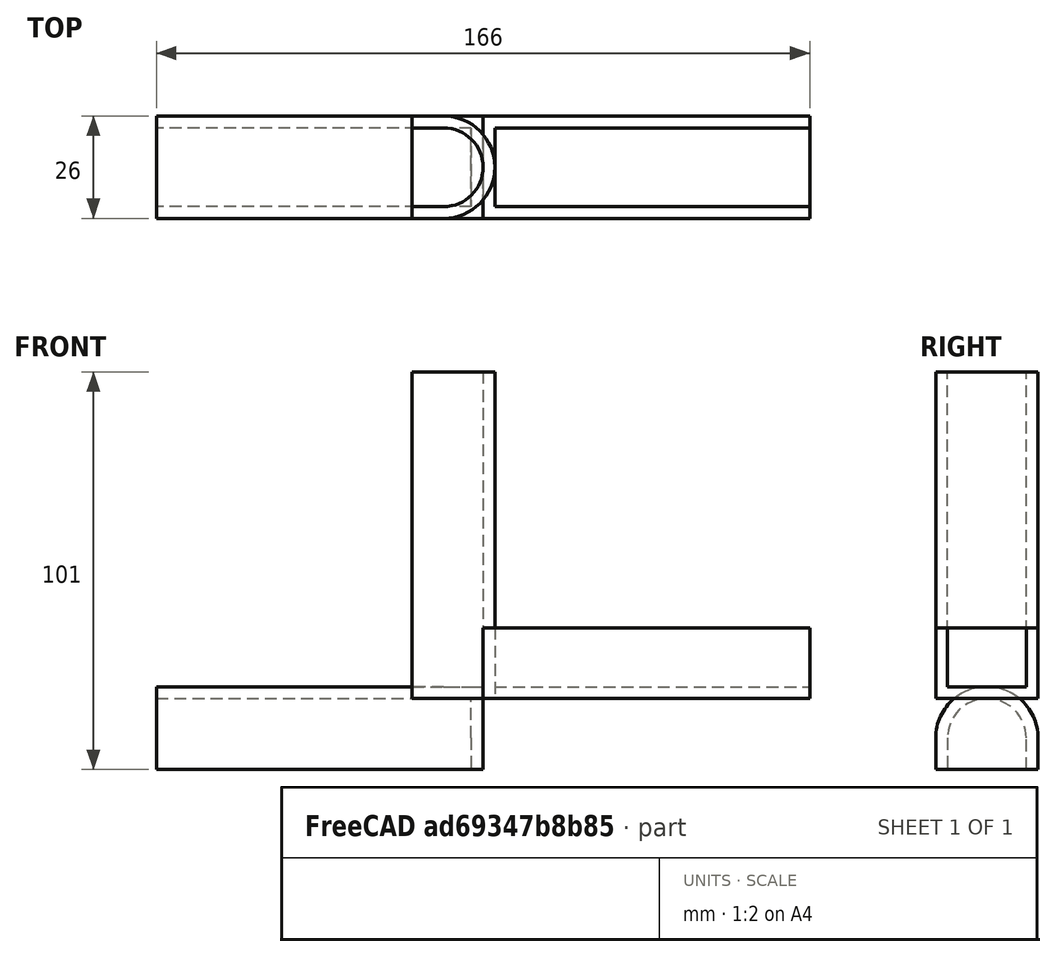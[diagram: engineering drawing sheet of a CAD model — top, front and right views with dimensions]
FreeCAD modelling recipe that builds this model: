
FCSTD DOCUMENT  (FreeCAD 0.16R6704 (Git))
Label: Peça
License: All rights reserved
LicenseURL: http://en.wikipedia.org/wiki/All_rights_reserved
objects: Part::Box×5, Part::Cylinder×3, Part::MultiFuse×2, Part::Feature×2, Part::Cut×2
note: 14 computed .brp shape members not serialized (recipe doc carries the construction recipe); baked Part::Feature solids carry a one-line shape summary decoded from their .brp

FEATURE [Part::Box] Box  label="BaseInferior"
  Height = 3
  Length = 83
  Width = 26
FEATURE [Part::Box] Box001  label="ParedeEsquerda"
  Height = 18
  Length = 83
  Width = 3
FEATURE [Part::Box] Box002  label="ParedeDireita"
  Height = 18
  Length = 83
  Placement = pos=(0,23,0) rot=(0,0,1;0rad)
  Width = 3
FEATURE [Part::Box] Box003  label="ParedeFundo"
  Height = 18
  Length = 3
  Width = 26
FEATURE [Part::MultiFuse] Fusion  label="Peça Unida - Sem Refinar"
  Shapes = -> [Box002,Box003,Box,Box001]
FEATURE [Part::Feature] Fusion001  label="Peça Final - Refinada - Sem Curvas"
  Placement = pos=(0,0,0) rot=(0,1,0;3.14159rad)
  shape: bbox 83 x 26 x 18 mm, 10 faces (baked)
FEATURE [Part::Cylinder] Cylinder  label="Cilindro"
  Angle = 180
  Height = 83
  Placement = pos=(-83,13,0) rot=(0.57735,0.57735,0.57735;2.0944rad)
  Radius = 13
FEATURE [Part::Cylinder] Cylinder001  label="Cilindro001"
  Angle = 180
  Height = 83
  Placement = pos=(-83,13,0) rot=(0.57735,0.57735,0.57735;2.0944rad)
  Radius = 10
FEATURE [Part::Cut] Cut
  Base = -> Cylinder
  Placement = pos=(0,0,-10) rot=(0,0,1;0rad)
  Tool = -> Cylinder001
FEATURE [Part::Box] Box004  label="Cubo"
  Height = 25
  Length = 83
  Placement = pos=(-83,0,-10) rot=(0,0,1;0rad)
  Width = 26
FEATURE [Part::Cut] Cut001
  Base = -> Fusion001
  Tool = -> Box004
FEATURE [Part::Cylinder] Cylinder002  label="Cilindro002"
  Angle = 180
  Height = 3
  Placement = pos=(-3,13,-10) rot=(0.57735,0.57735,0.57735;2.0944rad)
  Radius = 13
FEATURE [Part::MultiFuse] Fusion002
  Shapes = -> [Cylinder002,Cut001,Cut]
FEATURE [Part::Feature] Fusion002001  label="Fusion003"
  Placement = pos=(0,0,0) rot=(0,1,0;1.5708rad)
  shape: bbox 21 x 26 x 83 mm, 10 faces (baked)
